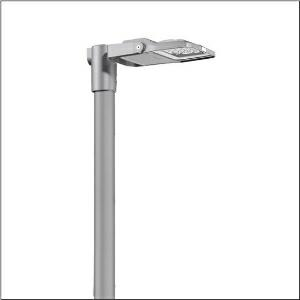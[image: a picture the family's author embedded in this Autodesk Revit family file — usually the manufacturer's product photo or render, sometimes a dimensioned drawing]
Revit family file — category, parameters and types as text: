
# Revit family: floodlight_fl_21_iq_micro___pl52_5xa7761a2d3a_8ecb
name_source: partatom
category: Lighting Fixtures
units: mm (PartAtom-declared; Revit-internal decimal feet)

## family parameters
Cut with Voids When Loaded = No
Host = Face
Light Source = No
Part Type = Normal
Room Calculation Point = No
Round Connector Dimension = Use Diameter
Shared = No

## types (1)
- --- (1 x LED, 2890 lm, 23.1 W, 3000K)
    Apparent Load = 23 VA
    CIE Flux Codes = 26 60 98 100 100
    Color Rendering = 70
    Color Temperature = 3000K
    Default Elevation = 1800 mm
    Description = Floodlight FL 21 iQ micro, floodlight, primary light control with lens, of PMMA, primary optical cover: protective disc, of toughened safety glass, transparent, light distribution: PL52, light emission: direct distribution, installation type: surface-mounted, lamps: LED, High Power LED, rated values: 2.890lm | 23,1W | 125,1lm/W (begin service life); end service life: 2.890lm | 23,8W; at 50% lumin. flux: 1.445lm | 11W | 131,4lm/W, colour temperature: 3000K, colour rendering: CRI > 70, light colour: 730, light setting 1 begin service life: 100% | 2.890lm | 23,1W | 125,1lm/W | 3.000K, light setting 1 end service life: 23,8W, further light settings possible, control: optimised constant luminous flux control (CLO 2.0), Desk-Remote (wireless, voltage-free reading and setting of iQ features in the workshop via application-optimized NFC function/RFID function), Light-Fading, Smart-Wire, Night-Set, Lumen-Switch, Temp-Guard, Auto-Match, pre-setting: linear dimming characteristic, with terminal, 6-pole, mains connection: 220..240V, AC, 50/60Hz, luminaire housing, of diecast aluminium, powder-coated, SITECO metallic grey (DB 702S), corrosivity category C5 mid according to DIN EN ISO 12944suitable for swimming poolschlorine-resistant, sealing non-destructively replaceable, please order mast flange separately, mast bracket, of steel, galvanised, powder-coated, SITECO metallic grey (DB 702S), protection rating (complete): IP66, insulation class (complete): insulation class II (safety insulation), certification: CE, ENEC, VDE, protection symbol: D, impact resistance: IK07, permissible operating ambient temperature: -40..+40°C, permissible operating ambient temperature for outdoor applications: -40..+50°C, standard: DIN EN 12944, LABS conformity tested according to VDMA 24364:2018-05, packaging unit: 1 piece

Light Distribution: PL52
    Height = 65 mm
    Lamp = 1 x LED
    Lamp Light Flux = 2890 lm
    Lamp Power = 23.1 W
    Lamp count = 1
    Length = 312 mm
    Luminous efficacy = 125 lm/W
    Manufacturer = Siteco
    ModVariant = No
    Model = 5XA7761A2D3A
    Number of Poles = 1
    OnlyDefault = Yes
    Power Factor = 1
    Product Name = Floodlight FL 21 iQ micro | PL52
    Product group = floodlight | pylon top
    ProductGroupID = 6101
    Protection Class = Protection class II
    Protection Degree = IP 66
    RLX_Detail_Level = 1
    RLX_Emergency_Light_Flux = 0 lm
    RLX_Emergency_Type = 0
    RLX_Emergency_Type_DB = No
    RlxData = <blob elided: 102197 chars, md5=0152b377>
    Socket = socket
    Standby Power = 0 W
    System Light Flux = 2890 lm
    System Power = 23 W
    Type Comments = factory setting: luminous flux: 100 % | dim-lin: 254 | 455 mA
    Type Image = l_1007121.jpg
    URL = http://relux.com
    VarID = @adj_177579
    Voltage = 0 V
    Weight = 0.00 kg
    Width = 230 mm

## geometry (parser evidence)
native form markers: Blend x4, Sweep x10
no freeform markers — native parametric forms only
